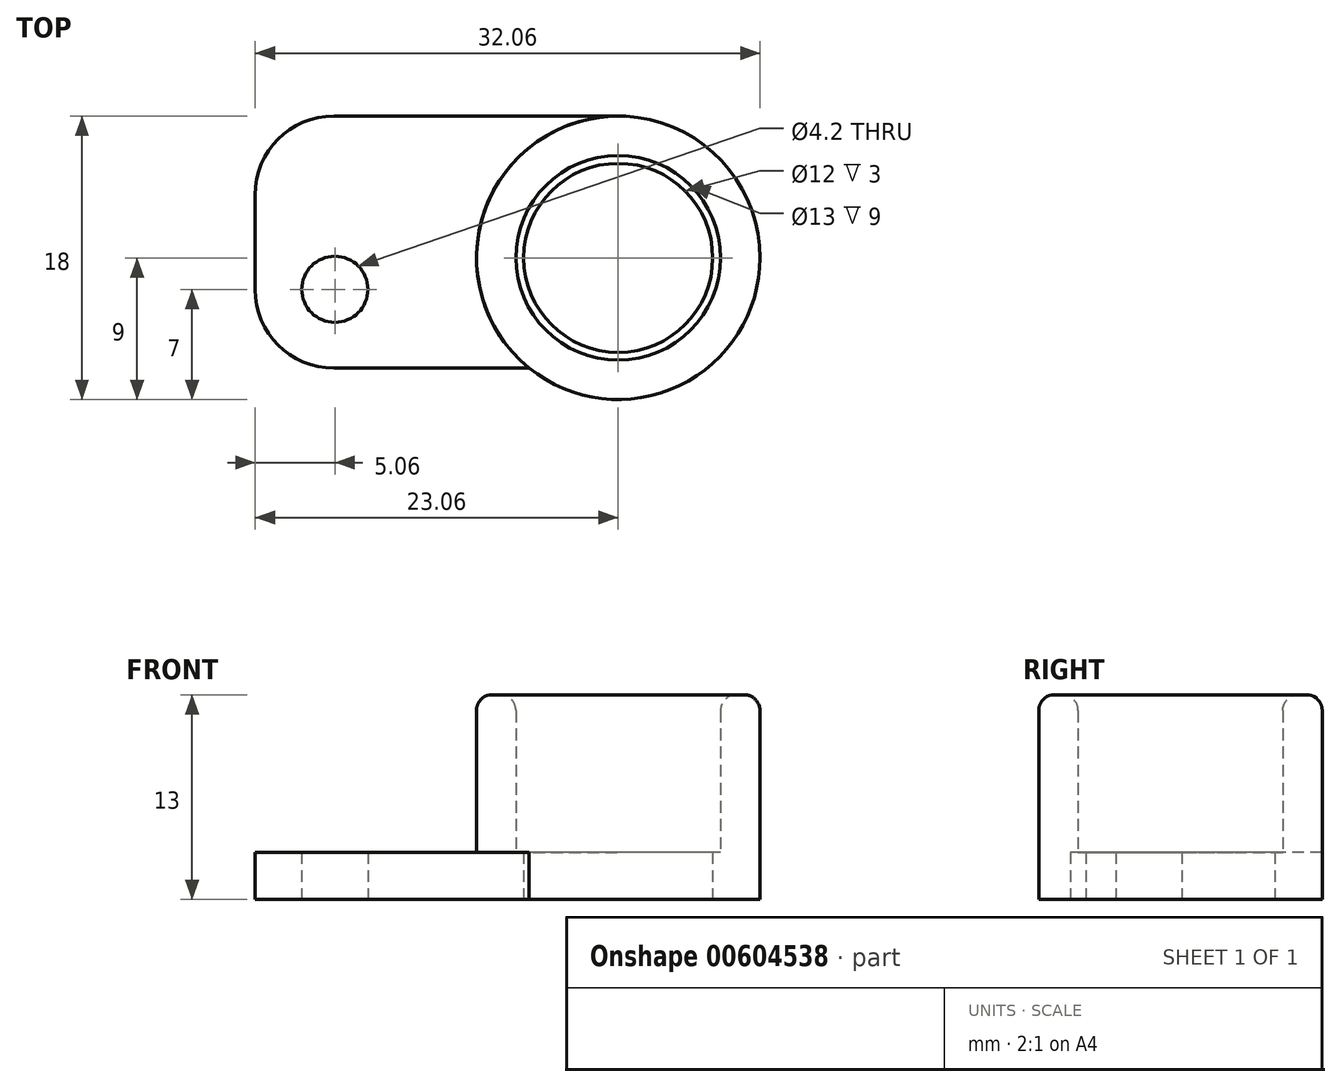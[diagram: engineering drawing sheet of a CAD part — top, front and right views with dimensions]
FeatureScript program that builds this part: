
annotation { "Feature Type Name" : "Feature", "Feature Type Description" : "" }
export const myFeature = defineFeature(function(context is Context, id is Id, definition is map)
    precondition{}
    {
        {
            var Q0;
            Q0=qCreatedBy(makeId("Top.planeOp"),FACE);
            var sketch = newSketch(context, id + "F0", { "sketchPlane" : qUnion([Q0])});
            skCircle(sketch, "E0", {"center": v(0, 0) * mm, "radius": 6 * mm});
            skCircle(sketch, "E1", {"center": v(0, 0) * mm, "radius": 9 * mm});
            skCircle(sketch, "E2", {"center": v(-18, -2) * mm, "radius": 2.1 * mm});
            skLineSegment(sketch, "E3.bottom", {"start": v(-23.06, -7) * mm, "end": v(0, -7) * mm});
            skLineSegment(sketch, "E3.top", {"start": v(-23.06, 9) * mm, "end": v(0, 9) * mm});
            skLineSegment(sketch, "E3.left", {"start": v(-23.06, -7) * mm, "end": v(-23.06, 9) * mm});
            skLineSegment(sketch, "E3.right", {"start": v(0, -7) * mm, "end": v(0, 9) * mm});
            skSolve(sketch);
        }
        {
            var Q0;
            Q0=makeQuery(id+"F0.imprint","IMPRINT",FACE,{"disambiguationData":[TD([[makeQuery(id+"F0.imprint","IMPRINT",EDGE,{"derivedFrom":sQuery(id+"F0.wireOp",EDGE,"E2")}),-1.0]])]});
            var Q1;
            {var subQ0=sQuery(id+"F0.wireOp",EDGE,"E3.right");var subQ3=sQuery(id+"F0.wireOp",EDGE,"E0");var subQ4=makeQuery(id+"F0.imprint","INTERSECT",VERTEX,{"disambiguationData":[OD(0.0)],"derivedFrom":[subQ3,subQ0]});Q1=makeQuery(id+"F0.imprint","IMPRINT",FACE,{"disambiguationData":[TD([[makeQuery(id+"F0.imprint","IMPRINT",EDGE,{"disambiguationData":[TD([[subQ4,1.0]])],"derivedFrom":subQ3}),-1.0]])]});}
            var Q2;
            {var subQ0=sQuery(id+"F0.wireOp",EDGE,"E3.right");var subQ3=sQuery(id+"F0.wireOp",EDGE,"E0");var subQ4=makeQuery(id+"F0.imprint","INTERSECT",VERTEX,{"disambiguationData":[OD(0.0)],"derivedFrom":[subQ3,subQ0]});Q2=makeQuery(id+"F0.imprint","IMPRINT",FACE,{"disambiguationData":[TD([[makeQuery(id+"F0.imprint","IMPRINT",EDGE,{"disambiguationData":[TD([[subQ4,-1.0]])],"derivedFrom":subQ3}),-1.0]])]});}
            extrude(context, id + "F1", {"entities" : qUnion([Q0, Q1, Q2]), "depth" : 3 * mm, "offsetDistance" : 25 * mm});
        }
        {
            var Q0;
            Q0=makeQuery(id+"F1.opExtrude","SWEPT_EDGE",EDGE,{"disambiguationData":[OSD([sQuery(id+"F0.wireOp",EDGE,"E3.top"),sQuery(id+"F0.wireOp",EDGE,"E3.left")])]});
            var Q1;
            Q1=makeQuery(id+"F1.opExtrude","SWEPT_EDGE",EDGE,{"disambiguationData":[OSD([sQuery(id+"F0.wireOp",EDGE,"E3.bottom"),sQuery(id+"F0.wireOp",EDGE,"E3.left")])]});
            fillet(context, id + "F2", {"entities" : qUnion([Q0, Q1]), "radius" : 5 * mm, "tangentPropagation" : true, "allowEdgeOverflow" : false});
        }
        {
            var Q0;
            Q0=makeQuery(id+"F1.opExtrude","CAP_FACE",FACE,{"disambiguationData":[OSD([sQuery(id+"F0.wireOp",EDGE,"E0"),sQuery(id+"F0.wireOp",EDGE,"E1"),sQuery(id+"F0.wireOp",EDGE,"E2"),sQuery(id+"F0.wireOp",EDGE,"E3.bottom"),sQuery(id+"F0.wireOp",EDGE,"E3.top"),sQuery(id+"F0.wireOp",EDGE,"E3.left")])],"isStart":false});
            var sketch = newSketch(context, id + "F3", { "sketchPlane" : qUnion([Q0])});
            skCircle(sketch, "E4", {"center": v(0, 0) * mm, "radius": 6.5 * mm});
            skCircle(sketch, "E5", {"center": v(0, 0) * mm, "radius": 9 * mm});
            skSolve(sketch);
        }
        {
            var Q0;
            Q0=makeQuery(id+"F3.imprint","IMPRINT",FACE,{"disambiguationData":[TD([[makeQuery(id+"F3.imprint","IMPRINT",EDGE,{"derivedFrom":sQuery(id+"F3.wireOp",EDGE,"E4")}),-1.0]])]});
            extrude(context, id + "F4", {"entities" : qUnion([Q0]), "operationType" : NewBodyOperationType.ADD, "depth" : 10 * mm, "offsetDistance" : 25 * mm});
        }
        {
            var Q0;
            Q0=makeQuery(id+"F4.opExtrude","CAP_EDGE",EDGE,{"disambiguationData":[OSD([sQuery(id+"F3.wireOp",EDGE,"E5")])],"isStart":false});
            var Q1;
            Q1=makeQuery(id+"F4.opExtrude","CAP_EDGE",EDGE,{"disambiguationData":[OSD([sQuery(id+"F3.wireOp",EDGE,"E4")])],"isStart":false});
            fillet(context, id + "F5", {"entities" : qUnion([Q0, Q1]), "radius" : 1 * mm, "tangentPropagation" : true, "allowEdgeOverflow" : false});
        }
    });
